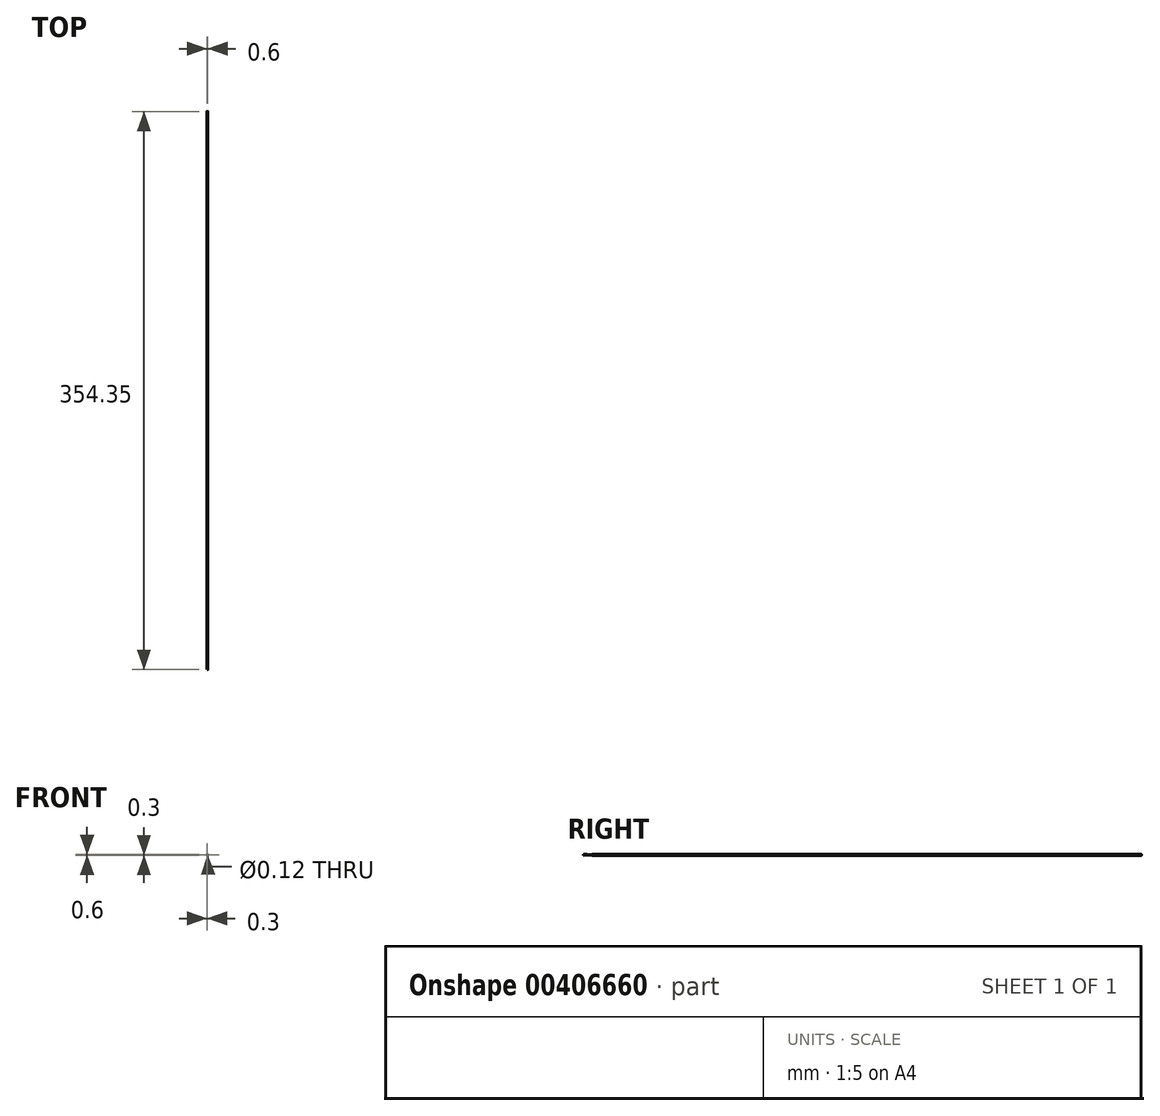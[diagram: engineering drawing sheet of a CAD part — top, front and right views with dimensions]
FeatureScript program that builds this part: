
annotation { "Feature Type Name" : "Feature", "Feature Type Description" : "" }
export const myFeature = defineFeature(function(context is Context, id is Id, definition is map)
    precondition{}
    {
        {
            var Q0;
            Q0=qCreatedBy(makeId("Top.planeOp"),FACE);
            var sketch = newSketch(context, id + "F0", { "sketchPlane" : qUnion([Q0])});
            skLineSegment(sketch, "E0", {"start": v(0, 0) * mm, "end": v(0, 25) * mm});
            skSolve(sketch);
        }
        {
            var Q0;
            Q0=qCreatedBy(makeId("Front.planeOp"),FACE);
            cPlane(context, id + "F1", {"entities" : qUnion([Q0]), "cplaneType" : CPlaneType.OFFSET, "offset" : 0.15 * mm, "oppositeDirection" : true, "width" : 150 * mm, "height" : 150 * mm});
        }
        {
            var Q0;
            Q0=qCreatedBy(id+"F1.planeOp",FACE);
            var sketch = newSketch(context, id + "F2", { "sketchPlane" : qUnion([Q0])});
            skCircle(sketch, "E1", {"center": v(0, 0) * mm, "radius": 0.06 * mm});
            skSolve(sketch);
        }
        {
            var Q0;
            Q0=qCreatedBy(makeId("Front.planeOp"),FACE);
            cPlane(context, id + "F3", {"entities" : qUnion([Q0]), "cplaneType" : CPlaneType.OFFSET, "offset" : 0.35 * mm, "oppositeDirection" : true, "width" : 150 * mm, "height" : 150 * mm});
        }
        {
            var Q0;
            Q0=qCreatedBy(id+"F3.planeOp",FACE);
            var sketch = newSketch(context, id + "F4", { "sketchPlane" : qUnion([Q0])});
            skCircle(sketch, "E2", {"center": v(0, 0) * mm, "radius": 0.06 * mm});
            skSolve(sketch);
        }
        {
            var Q0;
            Q0=qCreatedBy(makeId("Front.planeOp"),FACE);
            var Q1;
            Q1=qBodyType(qCreatedBy(id+"F6",EDGE),BodyType.WIRE);
            cPlane(context, id + "F5", {"entities" : qUnion([Q0, Q1]), "cplaneType" : CPlaneType.OFFSET, "offset" : 0.65 * mm, "oppositeDirection" : true, "width" : 150 * mm, "height" : 150 * mm});
        }
        {
            var Q0;
            Q0=qCreatedBy(id+"F5.planeOp",FACE);
            var sketch = newSketch(context, id + "F6", { "sketchPlane" : qUnion([Q0])});
            skCircle(sketch, "E3", {"center": v(0, 0) * mm, "radius": 0.06 * mm});
            skSolve(sketch);
        }
        {
            var Q0;
            Q0=makeQuery(id+"F2.imprint","IMPRINT",FACE,{"disambiguationData":[TD([[makeQuery(id+"F2.imprint","IMPRINT",EDGE,{"derivedFrom":sQuery(id+"F2.wireOp",EDGE,"E1")}),1.0]])]});
            var Q1;
            Q1=sQuery(id+"F2.wireOp",EDGE,"E1");
            extrude(context, id + "F7", {"entities" : qUnion([Q0]), "surfaceEntities" : qUnion([Q1]), "oppositeDirection" : true, "offsetDistance" : 25 * mm, "depth" : 0.2 * mm});
        }
        {
            var Q0;
            Q0=qSketchRegion(id+"F4",true);
            var Q1;
            Q1 = qSketchRegion(id + "FSffIr37tt4rMJt_3", true);
            extrude(context, id + "F8", {"entities" : qUnion([Q0, Q1]), "oppositeDirection" : true, "offsetDistance" : 25 * mm, "depth" : 0.3 * mm});
        }
        {
            var Q0;
            Q0=makeQuery(id+"F6.imprint","IMPRINT",FACE,{"disambiguationData":[TD([[makeQuery(id+"F6.imprint","IMPRINT",EDGE,{"derivedFrom":sQuery(id+"F6.wireOp",EDGE,"E3")}),1.0]])]});
            var Q1;
            Q1=sQuery(id+"F6.wireOp",EDGE,"E3");
            extrude(context, id + "F9", {"entities" : qUnion([Q0]), "surfaceEntities" : qUnion([Q1]), "oppositeDirection" : true, "depth" : 349.35 * mm});
        }
        {
            var Q0;
            Q0=qCreatedBy(makeId("Front.planeOp"),FACE);
            var Q1;
            Q1=qBodyType(qCreatedBy(id+"F11",EDGE),BodyType.WIRE);
            cPlane(context, id + "F10", {"entities" : qUnion([Q0, Q1]), "cplaneType" : CPlaneType.OFFSET, "offset" : 1 * mm, "oppositeDirection" : true, "width" : 150 * mm, "height" : 150 * mm});
        }
        {
            var Q0;
            Q0=qCreatedBy(id+"F10.planeOp",FACE);
            var sketch = newSketch(context, id + "F11", { "sketchPlane" : qUnion([Q0])});
            skCircle(sketch, "E4", {"center": v(0, 0) * mm, "radius": 0.06 * mm});
            skCircle(sketch, "E5.0", {"center": v(0, 0) * mm, "radius": 0.19 * mm});
            skSolve(sketch);
        }
        {
            var Q0;
            Q0=makeQuery(id+"F11.imprint","IMPRINT",FACE,{"disambiguationData":[TD([[makeQuery(id+"F11.imprint","IMPRINT",EDGE,{"derivedFrom":sQuery(id+"F11.wireOp",EDGE,"E4")}),-1.0]])]});
            extrude(context, id + "F12", {"entities" : qUnion([Q0]), "oppositeDirection" : true, "depth" : 349 * mm});
        }
        {
            var Q0;
            Q0=qCreatedBy(makeId("Right.planeOp"),FACE);
            var sketch = newSketch(context, id + "F13", { "sketchPlane" : qUnion([Q0])});
            skLineSegment(sketch, "E6", {"start": v(0.65, 0) * mm, "end": v(-4.35, 0) * mm});
            skLineSegment(sketch, "E7", {"start": v(0.65, 0) * mm, "end": v(0.35, 0.03) * mm});
            skFitSpline(sketch, "E8", {"points": [v(0.35, 0.03) * mm, v(0.23, 0.04) * mm, v(0.16, 0.05) * mm], "startDerivative": vector(-0.25, 0.03) * mm, "endDerivative": vector(-0.3, 0.01) * mm});
            skLineSegment(sketch, "E9", {"start": v(-4.35, 0) * mm, "end": v(-4.35, 0.3) * mm});
            skLineSegment(sketch, "E10", {"start": v(0.16, 0.05) * mm, "end": v(-4.35, 0.3) * mm});
            skSolve(sketch);
        }
        {
            var Q0;
            Q0 = qSketchRegion(id + "F13", true);
            var Q1;
            Q1=sQuery(id+"F13.wireOp",EDGE,"E6");
            revolve(context, id + "F14", {"surfaceOperationType" : NewSurfaceOperationType.NEW, "entities" : qUnion([Q0]), "axis" : qUnion([Q1]), "revolveType" : RevolveType.FULL});
        }
    });
